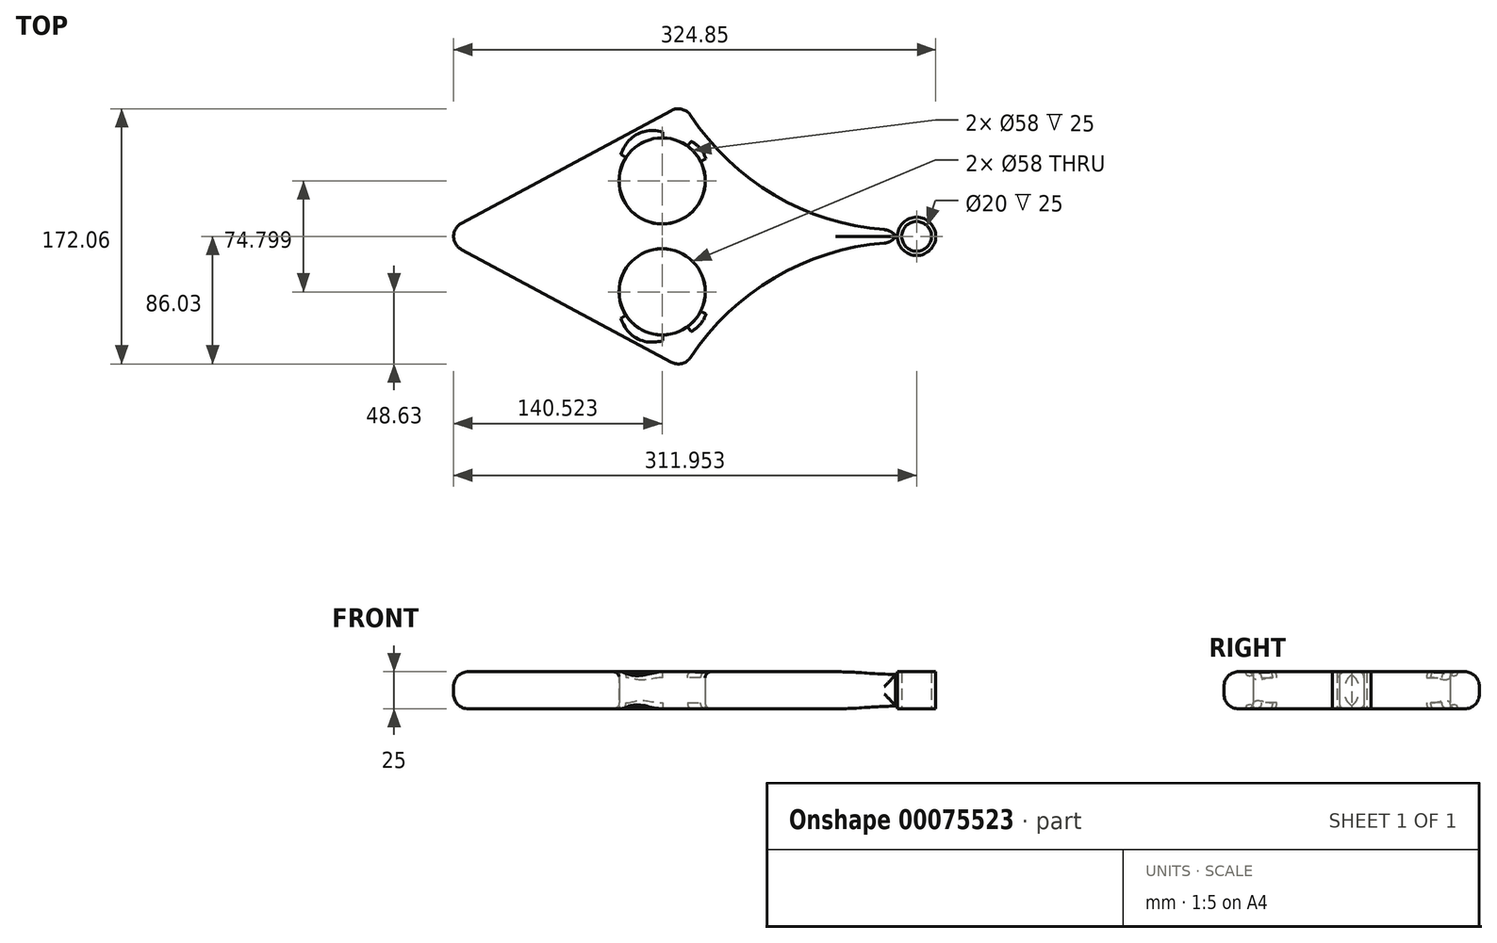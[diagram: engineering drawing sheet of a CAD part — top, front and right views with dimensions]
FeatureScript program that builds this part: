
annotation { "Feature Type Name" : "Feature", "Feature Type Description" : "" }
export const myFeature = defineFeature(function(context is Context, id is Id, definition is map)
    precondition{}
    {
        {
            var Q0;
            Q0=qCreatedBy(makeId("Top.planeOp"),FACE);
            var sketch = newSketch(context, id + "F0", { "sketchPlane" : qUnion([Q0])});
            skLineSegment(sketch, "E0", {"start": v(-166.02, 0) * mm, "end": v(0, 89.3) * mm});
            skArc(sketch, "E1", {"start": v(0, 89.3) * mm, "mid": v(61.16, 27.88) * mm, "end": v(144.5, 4.1) * mm});
            skLineSegment(sketch, "E2.MirrorCS", {"start": v(-166.02, 0) * mm, "end": v(0, -89.3) * mm});
            skArc(sketch, "E3.MirrorCS", {"start": v(0, -89.3) * mm, "mid": v(61.16, -27.88) * mm, "end": v(144.5, -4.1) * mm});
            skCircle(sketch, "E4", {"center": v(157.04, 0) * mm, "radius": 12.9 * mm});
            skArc(sketch, "E5", {"start": v(144.5, 4.1) * mm, "mid": v(144.03, 0) * mm, "end": v(144.5, -4.1) * mm});
            skSolve(sketch);
        }
        {
            var Q0;
            Q0=qCreatedBy(makeId("Top.planeOp"),FACE);
            var sketch = newSketch(context, id + "F1", { "sketchPlane" : qUnion([Q0])});
            skCircle(sketch, "E6", {"center": v(-14.39, 37.4) * mm, "radius": 29.07 * mm});
            skCircle(sketch, "E7.MirrorC", {"center": v(-14.39, -37.4) * mm, "radius": 29.07 * mm});
            skSolve(sketch);
        }
        {
            var Q0;
            Q0 = qSketchRegion(id + "F0", true);
            var Q1;
            Q1 = qSketchRegion(id + "F1", true);
            extrude(context, id + "F2", {"entities" : qUnion([Q0, Q1]), "depth" : 25 * mm});
        }
        {
            var Q0;
            Q0=sQuery(id+"F1.wireOp",VERTEX,"E7.MirrorC.center");
            var Q1;
            Q1=sQuery(id+"F1.wireOp",VERTEX,"E6.center");
            var Q2;
            Q2=makeQuery(id+"F2.opExtrude","SWEPT_BODY",BODY,{"disambiguationData":[OSD([sQuery(id+"F0.wireOp",EDGE,"E0"),sQuery(id+"F0.wireOp",EDGE,"E1"),sQuery(id+"F0.wireOp",EDGE,"E2.MirrorCS"),sQuery(id+"F0.wireOp",EDGE,"E3.MirrorCS"),sQuery(id+"F0.wireOp",EDGE,"E5")])]});
            var Q3;
            Q3=makeQuery(id+"F2.opExtrude","SWEPT_BODY",BODY,{"disambiguationData":[OSD([sQuery(id+"F1.wireOp",EDGE,"E7.MirrorC")])]});
            var Q4;
            Q4=makeQuery(id+"F2.opExtrude","SWEPT_BODY",BODY,{"disambiguationData":[OSD([sQuery(id+"F1.wireOp",EDGE,"E6")])]});
            hole(context, id + "F3", {"style" : HoleStyle.SIMPLE, "holeDiameter" : 58 * mm, "endStyle" : HoleEndStyle.THROUGH, "oppositeDirection" : true, "locations" : qUnion([Q0, Q1]), "scope" : qUnion([Q2, Q3, Q4])});
        }
        {
            var Q0;
            Q0=sQuery(id+"F0.wireOp",VERTEX,"E4.center");
            var Q1;
            Q1=makeQuery(id+"F2.opExtrude","SWEPT_BODY",BODY,{"disambiguationData":[OSD([sQuery(id+"F0.wireOp",EDGE,"E4")])]});
            hole(context, id + "F4", {"style" : HoleStyle.SIMPLE, "holeDiameter" : 20 * mm, "endStyle" : HoleEndStyle.THROUGH, "oppositeDirection" : true, "locations" : qUnion([Q0]), "scope" : qUnion([Q1])});
        }
        {
            var Q0;
            Q0=makeQuery(id+"F2.opExtrude","SWEPT_FACE",FACE,{"disambiguationData":[OSD([sQuery(id+"F0.wireOp",EDGE,"E2.MirrorCS")])]});
            var Q1;
            Q1=makeQuery(id+"F2.opExtrude","SWEPT_FACE",FACE,{"disambiguationData":[OSD([sQuery(id+"F0.wireOp",EDGE,"E3.MirrorCS")])]});
            var Q2;
            Q2=makeQuery(id+"F2.opExtrude","SWEPT_FACE",FACE,{"disambiguationData":[OSD([sQuery(id+"F0.wireOp",EDGE,"E0")])]});
            var Q3;
            Q3=makeQuery(id+"F2.opExtrude","SWEPT_FACE",FACE,{"disambiguationData":[OSD([sQuery(id+"F0.wireOp",EDGE,"E1")])]});
            fillet(context, id + "F5", {"entities" : qUnion([Q0, Q1, Q2, Q3]), "radius" : 10 * mm, "tangentPropagation" : true, "allowEdgeOverflow" : false});
        }
        {
            var Q0;
            Q0=makeQuery(id+"F2.opExtrude","CAP_FACE",FACE,{"disambiguationData":[OSD([sQuery(id+"F0.wireOp",EDGE,"E0"),sQuery(id+"F0.wireOp",EDGE,"E1"),sQuery(id+"F0.wireOp",EDGE,"E2.MirrorCS"),sQuery(id+"F0.wireOp",EDGE,"E3.MirrorCS"),sQuery(id+"F0.wireOp",EDGE,"E5")])],"isStart":false});
            var Q1;
            Q1=makeQuery(id+"F2.opExtrude","CAP_FACE",FACE,{"disambiguationData":[OSD([sQuery(id+"F0.wireOp",EDGE,"E0"),sQuery(id+"F0.wireOp",EDGE,"E1"),sQuery(id+"F0.wireOp",EDGE,"E2.MirrorCS"),sQuery(id+"F0.wireOp",EDGE,"E3.MirrorCS"),sQuery(id+"F0.wireOp",EDGE,"E5")])],"isStart":true});
            fillet(context, id + "F6", {"entities" : qUnion([Q0, Q1]), "radius" : 4 * mm, "tangentPropagation" : true, "allowEdgeOverflow" : false});
        }
    });
